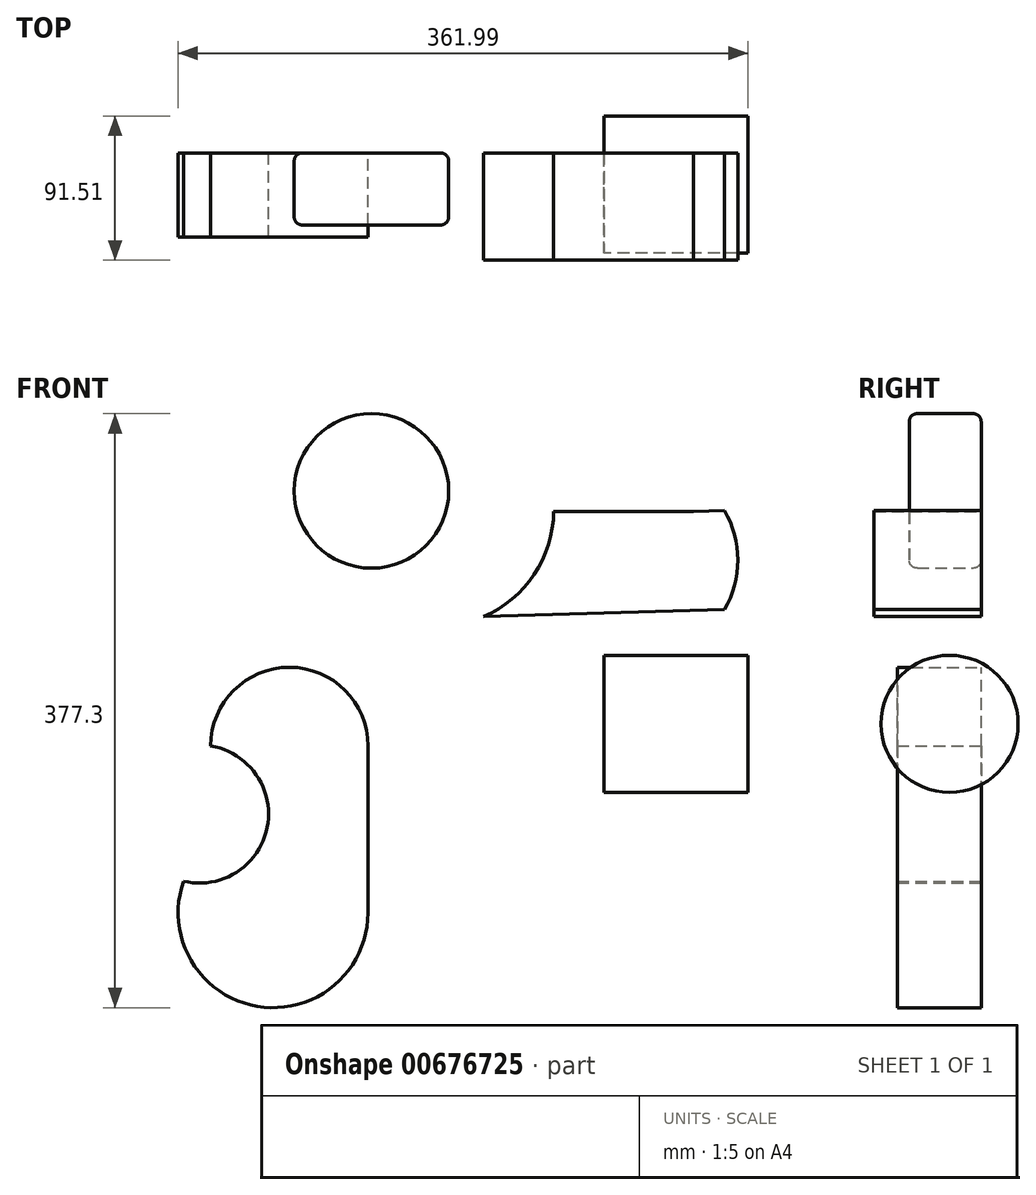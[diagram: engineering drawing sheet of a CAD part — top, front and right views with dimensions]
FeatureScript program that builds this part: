
annotation { "Feature Type Name" : "Feature", "Feature Type Description" : "" }
export const myFeature = defineFeature(function(context is Context, id is Id, definition is map)
    precondition{}
    {
        {
            var Q0;
            Q0=qCreatedBy(makeId("Front.planeOp"),FACE);
            var sketch = newSketch(context, id + "F0", { "sketchPlane" : qUnion([Q0])});
            skLineSegment(sketch, "E0", {"start": v(-76.53, -16.72) * mm, "end": v(76.53, -12.3) * mm});
            skLineSegment(sketch, "E1", {"start": v(-32, 50.2) * mm, "end": v(56.65, 50.2) * mm});
            skLineSegment(sketch, "E2", {"start": v(56.65, 50.2) * mm, "end": v(76.53, 50.77) * mm});
            skArc(sketch, "E3", {"start": v(-76.53, -16.72) * mm, "mid": v(-44.4, 10.17) * mm, "end": v(-32, 50.2) * mm});
            skArc(sketch, "E4", {"start": v(76.53, -12.3) * mm, "mid": v(84.99, 19.24) * mm, "end": v(76.53, 50.77) * mm});
            skSolve(sketch);
        }
        {
            var Q0;
            Q0 = qSketchRegion(id + "F0", true);
            extrude(context, id + "F1", {"entities" : qUnion([Q0]), "depth" : 68.07 * mm, "offsetDistance" : 25.4 * mm});
        }
        {
            var Q0;
            Q0=qCreatedBy(makeId("Front.planeOp"),FACE);
            var sketch = newSketch(context, id + "F2", { "sketchPlane" : qUnion([Q0])});
            skCircle(sketch, "E5", {"center": v(-147.77, 63.15) * mm, "radius": 49.07 * mm});
            skSolve(sketch);
        }
        {
            var Q0;
            Q0=makeQuery(id+"F2.imprint","IMPRINT",FACE,{"disambiguationData":[TD([[makeQuery(id+"F2.imprint","IMPRINT",EDGE,{"derivedFrom":sQuery(id+"F2.wireOp",EDGE,"E5")}),1.0]])]});
            extrude(context, id + "F3", {"entities" : qUnion([Q0]), "depth" : 45.72 * mm, "offsetDistance" : 25.4 * mm});
        }
        {
            var Q0;
            Q0=makeQuery(id+"F3.opExtrude","CAP_EDGE",EDGE,{"disambiguationData":[OSD([sQuery(id+"F2.wireOp",EDGE,"E5")])],"isStart":false});
            fillet(context, id + "F4", {"entities" : qUnion([Q0]), "radius" : 5.08 * mm, "tangentPropagation" : true, "allowEdgeOverflow" : false});
        }
        {
            var Q0;
            Q0=makeQuery(id+"F3.opExtrude","CAP_EDGE",EDGE,{"disambiguationData":[OSD([sQuery(id+"F2.wireOp",EDGE,"E5")])],"isStart":true});
            fillet(context, id + "F5", {"entities" : qUnion([Q0]), "radius" : 5.08 * mm, "tangentPropagation" : true, "allowEdgeOverflow" : false});
        }
        {
            var Q0;
            Q0=qCreatedBy(makeId("Right.planeOp"),FACE);
            var sketch = newSketch(context, id + "F6", { "sketchPlane" : qUnion([Q0])});
            skCircle(sketch, "E6", {"center": v(-20.1, -84.81) * mm, "radius": 43.53 * mm});
            skSolve(sketch);
        }
        {
            var Q0;
            Q0 = qSketchRegion(id + "F6", true);
            extrude(context, id + "F7", {"entities" : qUnion([Q0]), "depth" : 91.44 * mm, "offsetDistance" : 25.4 * mm});
        }
        {
            var Q0;
            Q0=qCreatedBy(makeId("Front.planeOp"),FACE);
            var sketch = newSketch(context, id + "F8", { "sketchPlane" : qUnion([Q0])});
            skLineSegment(sketch, "E7", {"start": v(-149.93, -98.82) * mm, "end": v(-149.93, -204.76) * mm});
            skArc(sketch, "E8", {"start": v(-149.93, -98.82) * mm, "mid": v(-199.89, -48.87) * mm, "end": v(-249.84, -98.82) * mm});
            skArc(sketch, "E9", {"start": v(-267.13, -184.75) * mm, "mid": v(-214.02, -150.73) * mm, "end": v(-249.84, -98.82) * mm});
            skArc(sketch, "E10", {"start": v(-267.13, -184.75) * mm, "mid": v(-220.39, -264.2) * mm, "end": v(-149.93, -204.76) * mm});
            skSolve(sketch);
        }
        {
            var Q0;
            Q0 = qSketchRegion(id + "F8", true);
            extrude(context, id + "F9", {"entities" : qUnion([Q0]), "depth" : 53.34 * mm, "offsetDistance" : 25.4 * mm});
        }
    });
